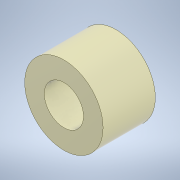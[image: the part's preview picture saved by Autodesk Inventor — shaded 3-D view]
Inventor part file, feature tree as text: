
AUTODESK INVENTOR PART (.ipt)
format: ipt  version: 2020.2 (Build 242310000, 310)  size: 102,400 bytes
history: native  units: mm
features: other x1, extrude x1, sketch x1
ambient origin geometry x8: Origin, YZ Plane, XZ Plane, XY Plane, X Axis, Y Axis, Z Axis, Center Point
bodies: Body1 (feature_tree)
feature tree (3):
  other  "ソリッド1"
  extrude  "押し出し1"  Depth=6.0mm
  sketch  "スケッチ1"
